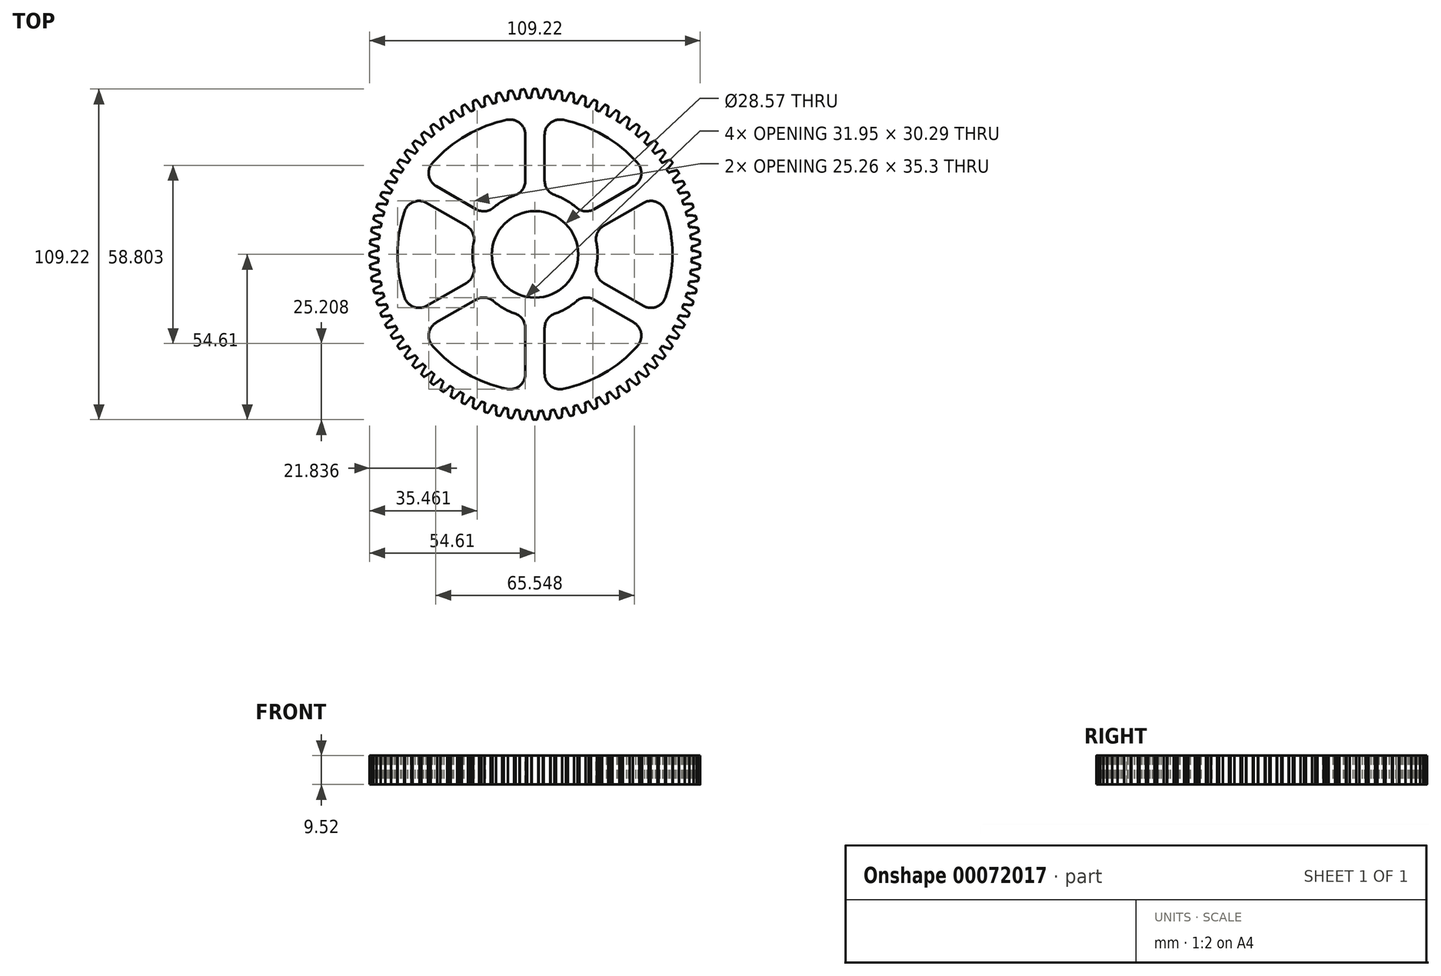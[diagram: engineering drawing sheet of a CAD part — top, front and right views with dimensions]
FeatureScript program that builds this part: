
annotation { "Feature Type Name" : "Feature", "Feature Type Description" : "" }
export const myFeature = defineFeature(function(context is Context, id is Id, definition is map)
    precondition{}
    {
        {
            var Q0;
            Q0=qCreatedBy(makeId("Top.planeOp"),FACE);
            var sketch = newSketch(context, id + "F0", { "sketchPlane" : qUnion([Q0])});
            skArc(sketch, "E0", {"start": v(1.25, 51.74) * mm, "mid": v(0, 51.75) * mm, "end": v(-1.25, 51.74) * mm});
            skArc(sketch, "E1", {"start": v(-1.25, -51.74) * mm, "mid": v(51.74, -1.25) * mm, "end": v(1.25, 51.74) * mm});
            skArc(sketch, "E2", {"start": v(-1.05, 53.12) * mm, "mid": v(-1.2, 52.43) * mm, "end": v(-1.25, 51.74) * mm});
            skArc(sketch, "E3", {"start": v(-0.67, 54.46) * mm, "mid": v(-0.86, 53.79) * mm, "end": v(-1.05, 53.12) * mm});
            skArc(sketch, "E4", {"start": v(-0.48, 54.6) * mm, "mid": v(-0.6, 54.57) * mm, "end": v(-0.67, 54.46) * mm});
            skArc(sketch, "E5", {"start": v(1.25, 51.74) * mm, "mid": v(1.2, 52.43) * mm, "end": v(1.05, 53.12) * mm});
            skArc(sketch, "E6", {"start": v(1.05, 53.12) * mm, "mid": v(0.86, 53.79) * mm, "end": v(0.67, 54.46) * mm});
            skArc(sketch, "E7", {"start": v(0.48, 54.6) * mm, "mid": v(0, 54.61) * mm, "end": v(-0.48, 54.6) * mm});
            skArc(sketch, "E8", {"start": v(0.67, 54.46) * mm, "mid": v(0.6, 54.57) * mm, "end": v(0.48, 54.6) * mm});
            skArc(sketch, "E9", {"start": v(-1.25, 51.74) * mm, "mid": v(-51.75, 0) * mm, "end": v(-1.25, -51.74) * mm});
            skSolve(sketch);
        }
        {
            var Q0;
            Q0=makeQuery(id+"F0.imprint","IMPRINT",FACE,{"disambiguationData":[TD([[makeQuery(id+"F0.imprint","IMPRINT",EDGE,{"derivedFrom":sQuery(id+"F0.wireOp",EDGE,"E0")}),1.0]])]});
            extrude(context, id + "F1", {"entities" : qUnion([Q0]), "endBound" : BoundingType.SYMMETRIC, "depth" : 9.52 * mm});
        }
        {
            var Q0;
            {var subQ0=sQuery(id+"F0.wireOp",EDGE,"E0");Q0=makeQuery(id+"F0.imprint","IMPRINT",FACE,{"disambiguationData":[TD([[makeQuery(id+"F0.imprint","IMPRINT",EDGE,{"derivedFrom":subQ0}),-1.0]])]});}
            var Q1;
            Q1=makeQuery(id+"F1.opExtrude","CAP_FACE",FACE,{"disambiguationData":[OSD([sQuery(id+"F0.wireOp",EDGE,"E0"),sQuery(id+"F0.wireOp",EDGE,"E1"),sQuery(id+"F0.wireOp",EDGE,"E9")])],"isStart":false});
            var Q2;
            Q2=makeQuery(id+"F1.opExtrude","CAP_FACE",FACE,{"disambiguationData":[OSD([sQuery(id+"F0.wireOp",EDGE,"E0"),sQuery(id+"F0.wireOp",EDGE,"E1"),sQuery(id+"F0.wireOp",EDGE,"E9")])],"isStart":true});
            extrude(context, id + "F2", {"entities" : qUnion([Q0]), "endBound" : BoundingType.UP_TO_SURFACE, "endBoundEntityFace" : qUnion([Q1]), "depth" : 25.4 * mm, "hasSecondDirection" : true, "secondDirectionBound" : SecondDirectionBoundingType.UP_TO_SURFACE, "secondDirectionOppositeDirection" : true, "secondDirectionBoundEntityFace" : qUnion([Q2]), "secondDirectionDepth" : 25.4 * mm});
        }
        {
            var Q0;
            Q0=makeQuery(id+"F2.opExtrude","SWEPT_BODY",BODY,{"disambiguationData":[OSD([sQuery(id+"F0.wireOp",EDGE,"E0"),sQuery(id+"F0.wireOp",EDGE,"E2"),sQuery(id+"F0.wireOp",EDGE,"E3"),sQuery(id+"F0.wireOp",EDGE,"E4"),sQuery(id+"F0.wireOp",EDGE,"E5"),sQuery(id+"F0.wireOp",EDGE,"E6"),sQuery(id+"F0.wireOp",EDGE,"E7"),sQuery(id+"F0.wireOp",EDGE,"E8")])]});
            var Q1;
            Q1=makeQuery(id+"F1.opExtrude","SWEPT_FACE",FACE,{"disambiguationData":[OSD([sQuery(id+"F0.wireOp",EDGE,"E0"),sQuery(id+"F0.wireOp",EDGE,"E1"),sQuery(id+"F0.wireOp",EDGE,"E9")])]});
            circularPattern(context, id + "F3", {"operationType" : NewBodyOperationType.ADD, "entities" : qUnion([Q0]), "axis" : qUnion([Q1]), "angle" : 360 * degree, "instanceCount" : round(84), "equalSpace" : true});
        }
        {
            var Q0;
            {var subQ0=sQuery(id+"F0.wireOp",EDGE,"E0");var subQ1=makeQuery(id+"F2.opExtrude","CAP_FACE",FACE,{"disambiguationData":[OSD([subQ0,sQuery(id+"F0.wireOp",EDGE,"E2"),sQuery(id+"F0.wireOp",EDGE,"E3"),sQuery(id+"F0.wireOp",EDGE,"E4"),sQuery(id+"F0.wireOp",EDGE,"E5"),sQuery(id+"F0.wireOp",EDGE,"E6"),sQuery(id+"F0.wireOp",EDGE,"E7"),sQuery(id+"F0.wireOp",EDGE,"E8")])],"isStart":false});Q0=makeQuery(id+"F3.boolean.opBoolean","MERGE",FACE,{"derivedFrom":[makeQuery(id+"F1.opExtrude","CAP_FACE",FACE,{"disambiguationData":[OSD([subQ0,sQuery(id+"F0.wireOp",EDGE,"E1"),sQuery(id+"F0.wireOp",EDGE,"E9")])],"isStart":false}),subQ1,makeQuery(id+"F3.opPattern","COPY",FACE,{"derivedFrom":subQ1,"instanceName":"1"}),makeQuery(id+"F3.opPattern","COPY",FACE,{"derivedFrom":subQ1,"instanceName":"2"}),makeQuery(id+"F3.opPattern","COPY",FACE,{"derivedFrom":subQ1,"instanceName":"3"}),makeQuery(id+"F3.opPattern","COPY",FACE,{"derivedFrom":subQ1,"instanceName":"4"}),makeQuery(id+"F3.opPattern","COPY",FACE,{"derivedFrom":subQ1,"instanceName":"5"}),makeQuery(id+"F3.opPattern","COPY",FACE,{"derivedFrom":subQ1,"instanceName":"6"}),makeQuery(id+"F3.opPattern","COPY",FACE,{"derivedFrom":subQ1,"instanceName":"7"}),makeQuery(id+"F3.opPattern","COPY",FACE,{"derivedFrom":subQ1,"instanceName":"8"}),makeQuery(id+"F3.opPattern","COPY",FACE,{"derivedFrom":subQ1,"instanceName":"9"}),makeQuery(id+"F3.opPattern","COPY",FACE,{"derivedFrom":subQ1,"instanceName":"10"}),makeQuery(id+"F3.opPattern","COPY",FACE,{"derivedFrom":subQ1,"instanceName":"11"}),makeQuery(id+"F3.opPattern","COPY",FACE,{"derivedFrom":subQ1,"instanceName":"12"}),makeQuery(id+"F3.opPattern","COPY",FACE,{"derivedFrom":subQ1,"instanceName":"13"}),makeQuery(id+"F3.opPattern","COPY",FACE,{"derivedFrom":subQ1,"instanceName":"14"}),makeQuery(id+"F3.opPattern","COPY",FACE,{"derivedFrom":subQ1,"instanceName":"15"}),makeQuery(id+"F3.opPattern","COPY",FACE,{"derivedFrom":subQ1,"instanceName":"16"}),makeQuery(id+"F3.opPattern","COPY",FACE,{"derivedFrom":subQ1,"instanceName":"17"}),makeQuery(id+"F3.opPattern","COPY",FACE,{"derivedFrom":subQ1,"instanceName":"18"}),makeQuery(id+"F3.opPattern","COPY",FACE,{"derivedFrom":subQ1,"instanceName":"19"}),makeQuery(id+"F3.opPattern","COPY",FACE,{"derivedFrom":subQ1,"instanceName":"20"}),makeQuery(id+"F3.opPattern","COPY",FACE,{"derivedFrom":subQ1,"instanceName":"21"}),makeQuery(id+"F3.opPattern","COPY",FACE,{"derivedFrom":subQ1,"instanceName":"22"}),makeQuery(id+"F3.opPattern","COPY",FACE,{"derivedFrom":subQ1,"instanceName":"23"}),makeQuery(id+"F3.opPattern","COPY",FACE,{"derivedFrom":subQ1,"instanceName":"24"}),makeQuery(id+"F3.opPattern","COPY",FACE,{"derivedFrom":subQ1,"instanceName":"25"}),makeQuery(id+"F3.opPattern","COPY",FACE,{"derivedFrom":subQ1,"instanceName":"26"}),makeQuery(id+"F3.opPattern","COPY",FACE,{"derivedFrom":subQ1,"instanceName":"27"}),makeQuery(id+"F3.opPattern","COPY",FACE,{"derivedFrom":subQ1,"instanceName":"28"}),makeQuery(id+"F3.opPattern","COPY",FACE,{"derivedFrom":subQ1,"instanceName":"29"}),makeQuery(id+"F3.opPattern","COPY",FACE,{"derivedFrom":subQ1,"instanceName":"30"}),makeQuery(id+"F3.opPattern","COPY",FACE,{"derivedFrom":subQ1,"instanceName":"31"}),makeQuery(id+"F3.opPattern","COPY",FACE,{"derivedFrom":subQ1,"instanceName":"32"}),makeQuery(id+"F3.opPattern","COPY",FACE,{"derivedFrom":subQ1,"instanceName":"33"}),makeQuery(id+"F3.opPattern","COPY",FACE,{"derivedFrom":subQ1,"instanceName":"34"}),makeQuery(id+"F3.opPattern","COPY",FACE,{"derivedFrom":subQ1,"instanceName":"35"}),makeQuery(id+"F3.opPattern","COPY",FACE,{"derivedFrom":subQ1,"instanceName":"36"}),makeQuery(id+"F3.opPattern","COPY",FACE,{"derivedFrom":subQ1,"instanceName":"37"}),makeQuery(id+"F3.opPattern","COPY",FACE,{"derivedFrom":subQ1,"instanceName":"38"}),makeQuery(id+"F3.opPattern","COPY",FACE,{"derivedFrom":subQ1,"instanceName":"39"}),makeQuery(id+"F3.opPattern","COPY",FACE,{"derivedFrom":subQ1,"instanceName":"40"}),makeQuery(id+"F3.opPattern","COPY",FACE,{"derivedFrom":subQ1,"instanceName":"41"}),makeQuery(id+"F3.opPattern","COPY",FACE,{"derivedFrom":subQ1,"instanceName":"42"}),makeQuery(id+"F3.opPattern","COPY",FACE,{"derivedFrom":subQ1,"instanceName":"43"}),makeQuery(id+"F3.opPattern","COPY",FACE,{"derivedFrom":subQ1,"instanceName":"44"}),makeQuery(id+"F3.opPattern","COPY",FACE,{"derivedFrom":subQ1,"instanceName":"45"}),makeQuery(id+"F3.opPattern","COPY",FACE,{"derivedFrom":subQ1,"instanceName":"46"}),makeQuery(id+"F3.opPattern","COPY",FACE,{"derivedFrom":subQ1,"instanceName":"47"}),makeQuery(id+"F3.opPattern","COPY",FACE,{"derivedFrom":subQ1,"instanceName":"48"}),makeQuery(id+"F3.opPattern","COPY",FACE,{"derivedFrom":subQ1,"instanceName":"49"}),makeQuery(id+"F3.opPattern","COPY",FACE,{"derivedFrom":subQ1,"instanceName":"50"}),makeQuery(id+"F3.opPattern","COPY",FACE,{"derivedFrom":subQ1,"instanceName":"51"}),makeQuery(id+"F3.opPattern","COPY",FACE,{"derivedFrom":subQ1,"instanceName":"52"}),makeQuery(id+"F3.opPattern","COPY",FACE,{"derivedFrom":subQ1,"instanceName":"53"}),makeQuery(id+"F3.opPattern","COPY",FACE,{"derivedFrom":subQ1,"instanceName":"54"}),makeQuery(id+"F3.opPattern","COPY",FACE,{"derivedFrom":subQ1,"instanceName":"55"}),makeQuery(id+"F3.opPattern","COPY",FACE,{"derivedFrom":subQ1,"instanceName":"56"}),makeQuery(id+"F3.opPattern","COPY",FACE,{"derivedFrom":subQ1,"instanceName":"57"}),makeQuery(id+"F3.opPattern","COPY",FACE,{"derivedFrom":subQ1,"instanceName":"58"}),makeQuery(id+"F3.opPattern","COPY",FACE,{"derivedFrom":subQ1,"instanceName":"59"}),makeQuery(id+"F3.opPattern","COPY",FACE,{"derivedFrom":subQ1,"instanceName":"60"}),makeQuery(id+"F3.opPattern","COPY",FACE,{"derivedFrom":subQ1,"instanceName":"61"}),makeQuery(id+"F3.opPattern","COPY",FACE,{"derivedFrom":subQ1,"instanceName":"62"}),makeQuery(id+"F3.opPattern","COPY",FACE,{"derivedFrom":subQ1,"instanceName":"63"}),makeQuery(id+"F3.opPattern","COPY",FACE,{"derivedFrom":subQ1,"instanceName":"64"}),makeQuery(id+"F3.opPattern","COPY",FACE,{"derivedFrom":subQ1,"instanceName":"65"}),makeQuery(id+"F3.opPattern","COPY",FACE,{"derivedFrom":subQ1,"instanceName":"66"}),makeQuery(id+"F3.opPattern","COPY",FACE,{"derivedFrom":subQ1,"instanceName":"67"}),makeQuery(id+"F3.opPattern","COPY",FACE,{"derivedFrom":subQ1,"instanceName":"68"}),makeQuery(id+"F3.opPattern","COPY",FACE,{"derivedFrom":subQ1,"instanceName":"69"}),makeQuery(id+"F3.opPattern","COPY",FACE,{"derivedFrom":subQ1,"instanceName":"70"}),makeQuery(id+"F3.opPattern","COPY",FACE,{"derivedFrom":subQ1,"instanceName":"71"}),makeQuery(id+"F3.opPattern","COPY",FACE,{"derivedFrom":subQ1,"instanceName":"72"}),makeQuery(id+"F3.opPattern","COPY",FACE,{"derivedFrom":subQ1,"instanceName":"73"}),makeQuery(id+"F3.opPattern","COPY",FACE,{"derivedFrom":subQ1,"instanceName":"74"}),makeQuery(id+"F3.opPattern","COPY",FACE,{"derivedFrom":subQ1,"instanceName":"75"}),makeQuery(id+"F3.opPattern","COPY",FACE,{"derivedFrom":subQ1,"instanceName":"76"}),makeQuery(id+"F3.opPattern","COPY",FACE,{"derivedFrom":subQ1,"instanceName":"77"}),makeQuery(id+"F3.opPattern","COPY",FACE,{"derivedFrom":subQ1,"instanceName":"78"}),makeQuery(id+"F3.opPattern","COPY",FACE,{"derivedFrom":subQ1,"instanceName":"79"}),makeQuery(id+"F3.opPattern","COPY",FACE,{"derivedFrom":subQ1,"instanceName":"80"}),makeQuery(id+"F3.opPattern","COPY",FACE,{"derivedFrom":subQ1,"instanceName":"81"}),makeQuery(id+"F3.opPattern","COPY",FACE,{"derivedFrom":subQ1,"instanceName":"82"}),makeQuery(id+"F3.opPattern","COPY",FACE,{"derivedFrom":subQ1,"instanceName":"83"})]});}
            var sketch = newSketch(context, id + "F4", { "sketchPlane" : qUnion([Q0])});
            skCircle(sketch, "E10", {"center": v(0, 0) * mm, "radius": 14.29 * mm});
            skSolve(sketch);
        }
        {
            var Q0;
            Q0=makeQuery(id+"F4.imprint","IMPRINT",FACE,{"disambiguationData":[TD([[makeQuery(id+"F4.imprint","IMPRINT",EDGE,{"derivedFrom":sQuery(id+"F4.wireOp",EDGE,"E10")}),1.0]])]});
            extrude(context, id + "F5", {"entities" : qUnion([Q0]), "operationType" : NewBodyOperationType.REMOVE, "endBound" : BoundingType.UP_TO_NEXT, "oppositeDirection" : true, "depth" : 25.4 * mm});
        }
        {
            var Q0;
            {var subQ0=sQuery(id+"F0.wireOp",EDGE,"E0");var subQ1=makeQuery(id+"F2.opExtrude","CAP_FACE",FACE,{"disambiguationData":[OSD([subQ0,sQuery(id+"F0.wireOp",EDGE,"E2"),sQuery(id+"F0.wireOp",EDGE,"E3"),sQuery(id+"F0.wireOp",EDGE,"E4"),sQuery(id+"F0.wireOp",EDGE,"E5"),sQuery(id+"F0.wireOp",EDGE,"E6"),sQuery(id+"F0.wireOp",EDGE,"E7"),sQuery(id+"F0.wireOp",EDGE,"E8")])],"isStart":false});Q0=makeQuery(id+"F3.boolean.opBoolean","MERGE",FACE,{"derivedFrom":[makeQuery(id+"F1.opExtrude","CAP_FACE",FACE,{"disambiguationData":[OSD([subQ0,sQuery(id+"F0.wireOp",EDGE,"E1"),sQuery(id+"F0.wireOp",EDGE,"E9")])],"isStart":false}),subQ1,makeQuery(id+"F3.opPattern","COPY",FACE,{"derivedFrom":subQ1,"instanceName":"1"}),makeQuery(id+"F3.opPattern","COPY",FACE,{"derivedFrom":subQ1,"instanceName":"2"}),makeQuery(id+"F3.opPattern","COPY",FACE,{"derivedFrom":subQ1,"instanceName":"3"}),makeQuery(id+"F3.opPattern","COPY",FACE,{"derivedFrom":subQ1,"instanceName":"4"}),makeQuery(id+"F3.opPattern","COPY",FACE,{"derivedFrom":subQ1,"instanceName":"5"}),makeQuery(id+"F3.opPattern","COPY",FACE,{"derivedFrom":subQ1,"instanceName":"6"}),makeQuery(id+"F3.opPattern","COPY",FACE,{"derivedFrom":subQ1,"instanceName":"7"}),makeQuery(id+"F3.opPattern","COPY",FACE,{"derivedFrom":subQ1,"instanceName":"8"}),makeQuery(id+"F3.opPattern","COPY",FACE,{"derivedFrom":subQ1,"instanceName":"9"}),makeQuery(id+"F3.opPattern","COPY",FACE,{"derivedFrom":subQ1,"instanceName":"10"}),makeQuery(id+"F3.opPattern","COPY",FACE,{"derivedFrom":subQ1,"instanceName":"11"}),makeQuery(id+"F3.opPattern","COPY",FACE,{"derivedFrom":subQ1,"instanceName":"12"}),makeQuery(id+"F3.opPattern","COPY",FACE,{"derivedFrom":subQ1,"instanceName":"13"}),makeQuery(id+"F3.opPattern","COPY",FACE,{"derivedFrom":subQ1,"instanceName":"14"}),makeQuery(id+"F3.opPattern","COPY",FACE,{"derivedFrom":subQ1,"instanceName":"15"}),makeQuery(id+"F3.opPattern","COPY",FACE,{"derivedFrom":subQ1,"instanceName":"16"}),makeQuery(id+"F3.opPattern","COPY",FACE,{"derivedFrom":subQ1,"instanceName":"17"}),makeQuery(id+"F3.opPattern","COPY",FACE,{"derivedFrom":subQ1,"instanceName":"18"}),makeQuery(id+"F3.opPattern","COPY",FACE,{"derivedFrom":subQ1,"instanceName":"19"}),makeQuery(id+"F3.opPattern","COPY",FACE,{"derivedFrom":subQ1,"instanceName":"20"}),makeQuery(id+"F3.opPattern","COPY",FACE,{"derivedFrom":subQ1,"instanceName":"21"}),makeQuery(id+"F3.opPattern","COPY",FACE,{"derivedFrom":subQ1,"instanceName":"22"}),makeQuery(id+"F3.opPattern","COPY",FACE,{"derivedFrom":subQ1,"instanceName":"23"}),makeQuery(id+"F3.opPattern","COPY",FACE,{"derivedFrom":subQ1,"instanceName":"24"}),makeQuery(id+"F3.opPattern","COPY",FACE,{"derivedFrom":subQ1,"instanceName":"25"}),makeQuery(id+"F3.opPattern","COPY",FACE,{"derivedFrom":subQ1,"instanceName":"26"}),makeQuery(id+"F3.opPattern","COPY",FACE,{"derivedFrom":subQ1,"instanceName":"27"}),makeQuery(id+"F3.opPattern","COPY",FACE,{"derivedFrom":subQ1,"instanceName":"28"}),makeQuery(id+"F3.opPattern","COPY",FACE,{"derivedFrom":subQ1,"instanceName":"29"}),makeQuery(id+"F3.opPattern","COPY",FACE,{"derivedFrom":subQ1,"instanceName":"30"}),makeQuery(id+"F3.opPattern","COPY",FACE,{"derivedFrom":subQ1,"instanceName":"31"}),makeQuery(id+"F3.opPattern","COPY",FACE,{"derivedFrom":subQ1,"instanceName":"32"}),makeQuery(id+"F3.opPattern","COPY",FACE,{"derivedFrom":subQ1,"instanceName":"33"}),makeQuery(id+"F3.opPattern","COPY",FACE,{"derivedFrom":subQ1,"instanceName":"34"}),makeQuery(id+"F3.opPattern","COPY",FACE,{"derivedFrom":subQ1,"instanceName":"35"}),makeQuery(id+"F3.opPattern","COPY",FACE,{"derivedFrom":subQ1,"instanceName":"36"}),makeQuery(id+"F3.opPattern","COPY",FACE,{"derivedFrom":subQ1,"instanceName":"37"}),makeQuery(id+"F3.opPattern","COPY",FACE,{"derivedFrom":subQ1,"instanceName":"38"}),makeQuery(id+"F3.opPattern","COPY",FACE,{"derivedFrom":subQ1,"instanceName":"39"}),makeQuery(id+"F3.opPattern","COPY",FACE,{"derivedFrom":subQ1,"instanceName":"40"}),makeQuery(id+"F3.opPattern","COPY",FACE,{"derivedFrom":subQ1,"instanceName":"41"}),makeQuery(id+"F3.opPattern","COPY",FACE,{"derivedFrom":subQ1,"instanceName":"42"}),makeQuery(id+"F3.opPattern","COPY",FACE,{"derivedFrom":subQ1,"instanceName":"43"}),makeQuery(id+"F3.opPattern","COPY",FACE,{"derivedFrom":subQ1,"instanceName":"44"}),makeQuery(id+"F3.opPattern","COPY",FACE,{"derivedFrom":subQ1,"instanceName":"45"}),makeQuery(id+"F3.opPattern","COPY",FACE,{"derivedFrom":subQ1,"instanceName":"46"}),makeQuery(id+"F3.opPattern","COPY",FACE,{"derivedFrom":subQ1,"instanceName":"47"}),makeQuery(id+"F3.opPattern","COPY",FACE,{"derivedFrom":subQ1,"instanceName":"48"}),makeQuery(id+"F3.opPattern","COPY",FACE,{"derivedFrom":subQ1,"instanceName":"49"}),makeQuery(id+"F3.opPattern","COPY",FACE,{"derivedFrom":subQ1,"instanceName":"50"}),makeQuery(id+"F3.opPattern","COPY",FACE,{"derivedFrom":subQ1,"instanceName":"51"}),makeQuery(id+"F3.opPattern","COPY",FACE,{"derivedFrom":subQ1,"instanceName":"52"}),makeQuery(id+"F3.opPattern","COPY",FACE,{"derivedFrom":subQ1,"instanceName":"53"}),makeQuery(id+"F3.opPattern","COPY",FACE,{"derivedFrom":subQ1,"instanceName":"54"}),makeQuery(id+"F3.opPattern","COPY",FACE,{"derivedFrom":subQ1,"instanceName":"55"}),makeQuery(id+"F3.opPattern","COPY",FACE,{"derivedFrom":subQ1,"instanceName":"56"}),makeQuery(id+"F3.opPattern","COPY",FACE,{"derivedFrom":subQ1,"instanceName":"57"}),makeQuery(id+"F3.opPattern","COPY",FACE,{"derivedFrom":subQ1,"instanceName":"58"}),makeQuery(id+"F3.opPattern","COPY",FACE,{"derivedFrom":subQ1,"instanceName":"59"}),makeQuery(id+"F3.opPattern","COPY",FACE,{"derivedFrom":subQ1,"instanceName":"60"}),makeQuery(id+"F3.opPattern","COPY",FACE,{"derivedFrom":subQ1,"instanceName":"61"}),makeQuery(id+"F3.opPattern","COPY",FACE,{"derivedFrom":subQ1,"instanceName":"62"}),makeQuery(id+"F3.opPattern","COPY",FACE,{"derivedFrom":subQ1,"instanceName":"63"}),makeQuery(id+"F3.opPattern","COPY",FACE,{"derivedFrom":subQ1,"instanceName":"64"}),makeQuery(id+"F3.opPattern","COPY",FACE,{"derivedFrom":subQ1,"instanceName":"65"}),makeQuery(id+"F3.opPattern","COPY",FACE,{"derivedFrom":subQ1,"instanceName":"66"}),makeQuery(id+"F3.opPattern","COPY",FACE,{"derivedFrom":subQ1,"instanceName":"67"}),makeQuery(id+"F3.opPattern","COPY",FACE,{"derivedFrom":subQ1,"instanceName":"68"}),makeQuery(id+"F3.opPattern","COPY",FACE,{"derivedFrom":subQ1,"instanceName":"69"}),makeQuery(id+"F3.opPattern","COPY",FACE,{"derivedFrom":subQ1,"instanceName":"70"}),makeQuery(id+"F3.opPattern","COPY",FACE,{"derivedFrom":subQ1,"instanceName":"71"}),makeQuery(id+"F3.opPattern","COPY",FACE,{"derivedFrom":subQ1,"instanceName":"72"}),makeQuery(id+"F3.opPattern","COPY",FACE,{"derivedFrom":subQ1,"instanceName":"73"}),makeQuery(id+"F3.opPattern","COPY",FACE,{"derivedFrom":subQ1,"instanceName":"74"}),makeQuery(id+"F3.opPattern","COPY",FACE,{"derivedFrom":subQ1,"instanceName":"75"}),makeQuery(id+"F3.opPattern","COPY",FACE,{"derivedFrom":subQ1,"instanceName":"76"}),makeQuery(id+"F3.opPattern","COPY",FACE,{"derivedFrom":subQ1,"instanceName":"77"}),makeQuery(id+"F3.opPattern","COPY",FACE,{"derivedFrom":subQ1,"instanceName":"78"}),makeQuery(id+"F3.opPattern","COPY",FACE,{"derivedFrom":subQ1,"instanceName":"79"}),makeQuery(id+"F3.opPattern","COPY",FACE,{"derivedFrom":subQ1,"instanceName":"80"}),makeQuery(id+"F3.opPattern","COPY",FACE,{"derivedFrom":subQ1,"instanceName":"81"}),makeQuery(id+"F3.opPattern","COPY",FACE,{"derivedFrom":subQ1,"instanceName":"82"}),makeQuery(id+"F3.opPattern","COPY",FACE,{"derivedFrom":subQ1,"instanceName":"83"})]});}
            var sketch = newSketch(context, id + "F6", { "sketchPlane" : qUnion([Q0])});
            skArc(sketch, "E11", {"start": v(0, 20.64) * mm, "mid": v(-10.32, 17.87) * mm, "end": v(-17.87, 10.32) * mm});
            skArc(sketch, "E12", {"start": v(0, 45.4) * mm, "mid": v(-22.7, 39.32) * mm, "end": v(-39.32, 22.7) * mm});
            skLineSegment(sketch, "E13", {"start": v(0, 20.64) * mm, "end": v(0, 45.4) * mm, "construction": true});
            skLineSegment(sketch, "E14", {"start": v(-17.87, 10.32) * mm, "end": v(-39.32, 22.7) * mm, "construction": true});
            skLineSegment(sketch, "E15.0", {"start": v(-16.07, 12.95) * mm, "end": v(-37.64, 25.4) * mm});
            skLineSegment(sketch, "E16.0", {"start": v(-3.18, 20.4) * mm, "end": v(-3.18, 45.3) * mm});
            skSolve(sketch);
        }
        {
            var Q0;
            {var subQ0=sQuery(id+"F6.wireOp",EDGE,"E15.0");Q0=makeQuery(id+"F6.imprint","IMPRINT",FACE,{"disambiguationData":[TD([[makeQuery(id+"F6.imprint","IMPRINT",EDGE,{"derivedFrom":subQ0}),-1.0]])]});}
            var Q1;
            {var subQ0=sQuery(id+"F0.wireOp",EDGE,"E0");var subQ1=makeQuery(id+"F2.opExtrude","CAP_FACE",FACE,{"disambiguationData":[OSD([subQ0,sQuery(id+"F0.wireOp",EDGE,"E2"),sQuery(id+"F0.wireOp",EDGE,"E3"),sQuery(id+"F0.wireOp",EDGE,"E4"),sQuery(id+"F0.wireOp",EDGE,"E5"),sQuery(id+"F0.wireOp",EDGE,"E6"),sQuery(id+"F0.wireOp",EDGE,"E7"),sQuery(id+"F0.wireOp",EDGE,"E8")])],"isStart":true});Q1=makeQuery(id+"F3.boolean.opBoolean","MERGE",FACE,{"derivedFrom":[makeQuery(id+"F1.opExtrude","CAP_FACE",FACE,{"disambiguationData":[OSD([subQ0,sQuery(id+"F0.wireOp",EDGE,"E1"),sQuery(id+"F0.wireOp",EDGE,"E9")])],"isStart":true}),subQ1,makeQuery(id+"F3.opPattern","COPY",FACE,{"derivedFrom":subQ1,"instanceName":"1"}),makeQuery(id+"F3.opPattern","COPY",FACE,{"derivedFrom":subQ1,"instanceName":"2"}),makeQuery(id+"F3.opPattern","COPY",FACE,{"derivedFrom":subQ1,"instanceName":"3"}),makeQuery(id+"F3.opPattern","COPY",FACE,{"derivedFrom":subQ1,"instanceName":"4"}),makeQuery(id+"F3.opPattern","COPY",FACE,{"derivedFrom":subQ1,"instanceName":"5"}),makeQuery(id+"F3.opPattern","COPY",FACE,{"derivedFrom":subQ1,"instanceName":"6"}),makeQuery(id+"F3.opPattern","COPY",FACE,{"derivedFrom":subQ1,"instanceName":"7"}),makeQuery(id+"F3.opPattern","COPY",FACE,{"derivedFrom":subQ1,"instanceName":"8"}),makeQuery(id+"F3.opPattern","COPY",FACE,{"derivedFrom":subQ1,"instanceName":"9"}),makeQuery(id+"F3.opPattern","COPY",FACE,{"derivedFrom":subQ1,"instanceName":"10"}),makeQuery(id+"F3.opPattern","COPY",FACE,{"derivedFrom":subQ1,"instanceName":"11"}),makeQuery(id+"F3.opPattern","COPY",FACE,{"derivedFrom":subQ1,"instanceName":"12"}),makeQuery(id+"F3.opPattern","COPY",FACE,{"derivedFrom":subQ1,"instanceName":"13"}),makeQuery(id+"F3.opPattern","COPY",FACE,{"derivedFrom":subQ1,"instanceName":"14"}),makeQuery(id+"F3.opPattern","COPY",FACE,{"derivedFrom":subQ1,"instanceName":"15"}),makeQuery(id+"F3.opPattern","COPY",FACE,{"derivedFrom":subQ1,"instanceName":"16"}),makeQuery(id+"F3.opPattern","COPY",FACE,{"derivedFrom":subQ1,"instanceName":"17"}),makeQuery(id+"F3.opPattern","COPY",FACE,{"derivedFrom":subQ1,"instanceName":"18"}),makeQuery(id+"F3.opPattern","COPY",FACE,{"derivedFrom":subQ1,"instanceName":"19"}),makeQuery(id+"F3.opPattern","COPY",FACE,{"derivedFrom":subQ1,"instanceName":"20"}),makeQuery(id+"F3.opPattern","COPY",FACE,{"derivedFrom":subQ1,"instanceName":"21"}),makeQuery(id+"F3.opPattern","COPY",FACE,{"derivedFrom":subQ1,"instanceName":"22"}),makeQuery(id+"F3.opPattern","COPY",FACE,{"derivedFrom":subQ1,"instanceName":"23"}),makeQuery(id+"F3.opPattern","COPY",FACE,{"derivedFrom":subQ1,"instanceName":"24"}),makeQuery(id+"F3.opPattern","COPY",FACE,{"derivedFrom":subQ1,"instanceName":"25"}),makeQuery(id+"F3.opPattern","COPY",FACE,{"derivedFrom":subQ1,"instanceName":"26"}),makeQuery(id+"F3.opPattern","COPY",FACE,{"derivedFrom":subQ1,"instanceName":"27"}),makeQuery(id+"F3.opPattern","COPY",FACE,{"derivedFrom":subQ1,"instanceName":"28"}),makeQuery(id+"F3.opPattern","COPY",FACE,{"derivedFrom":subQ1,"instanceName":"29"}),makeQuery(id+"F3.opPattern","COPY",FACE,{"derivedFrom":subQ1,"instanceName":"30"}),makeQuery(id+"F3.opPattern","COPY",FACE,{"derivedFrom":subQ1,"instanceName":"31"}),makeQuery(id+"F3.opPattern","COPY",FACE,{"derivedFrom":subQ1,"instanceName":"32"}),makeQuery(id+"F3.opPattern","COPY",FACE,{"derivedFrom":subQ1,"instanceName":"33"}),makeQuery(id+"F3.opPattern","COPY",FACE,{"derivedFrom":subQ1,"instanceName":"34"}),makeQuery(id+"F3.opPattern","COPY",FACE,{"derivedFrom":subQ1,"instanceName":"35"}),makeQuery(id+"F3.opPattern","COPY",FACE,{"derivedFrom":subQ1,"instanceName":"36"}),makeQuery(id+"F3.opPattern","COPY",FACE,{"derivedFrom":subQ1,"instanceName":"37"}),makeQuery(id+"F3.opPattern","COPY",FACE,{"derivedFrom":subQ1,"instanceName":"38"}),makeQuery(id+"F3.opPattern","COPY",FACE,{"derivedFrom":subQ1,"instanceName":"39"}),makeQuery(id+"F3.opPattern","COPY",FACE,{"derivedFrom":subQ1,"instanceName":"40"}),makeQuery(id+"F3.opPattern","COPY",FACE,{"derivedFrom":subQ1,"instanceName":"41"}),makeQuery(id+"F3.opPattern","COPY",FACE,{"derivedFrom":subQ1,"instanceName":"42"}),makeQuery(id+"F3.opPattern","COPY",FACE,{"derivedFrom":subQ1,"instanceName":"43"}),makeQuery(id+"F3.opPattern","COPY",FACE,{"derivedFrom":subQ1,"instanceName":"44"}),makeQuery(id+"F3.opPattern","COPY",FACE,{"derivedFrom":subQ1,"instanceName":"45"}),makeQuery(id+"F3.opPattern","COPY",FACE,{"derivedFrom":subQ1,"instanceName":"46"}),makeQuery(id+"F3.opPattern","COPY",FACE,{"derivedFrom":subQ1,"instanceName":"47"}),makeQuery(id+"F3.opPattern","COPY",FACE,{"derivedFrom":subQ1,"instanceName":"48"}),makeQuery(id+"F3.opPattern","COPY",FACE,{"derivedFrom":subQ1,"instanceName":"49"}),makeQuery(id+"F3.opPattern","COPY",FACE,{"derivedFrom":subQ1,"instanceName":"50"}),makeQuery(id+"F3.opPattern","COPY",FACE,{"derivedFrom":subQ1,"instanceName":"51"}),makeQuery(id+"F3.opPattern","COPY",FACE,{"derivedFrom":subQ1,"instanceName":"52"}),makeQuery(id+"F3.opPattern","COPY",FACE,{"derivedFrom":subQ1,"instanceName":"53"}),makeQuery(id+"F3.opPattern","COPY",FACE,{"derivedFrom":subQ1,"instanceName":"54"}),makeQuery(id+"F3.opPattern","COPY",FACE,{"derivedFrom":subQ1,"instanceName":"55"}),makeQuery(id+"F3.opPattern","COPY",FACE,{"derivedFrom":subQ1,"instanceName":"56"}),makeQuery(id+"F3.opPattern","COPY",FACE,{"derivedFrom":subQ1,"instanceName":"57"}),makeQuery(id+"F3.opPattern","COPY",FACE,{"derivedFrom":subQ1,"instanceName":"58"}),makeQuery(id+"F3.opPattern","COPY",FACE,{"derivedFrom":subQ1,"instanceName":"59"}),makeQuery(id+"F3.opPattern","COPY",FACE,{"derivedFrom":subQ1,"instanceName":"60"}),makeQuery(id+"F3.opPattern","COPY",FACE,{"derivedFrom":subQ1,"instanceName":"61"}),makeQuery(id+"F3.opPattern","COPY",FACE,{"derivedFrom":subQ1,"instanceName":"62"}),makeQuery(id+"F3.opPattern","COPY",FACE,{"derivedFrom":subQ1,"instanceName":"63"}),makeQuery(id+"F3.opPattern","COPY",FACE,{"derivedFrom":subQ1,"instanceName":"64"}),makeQuery(id+"F3.opPattern","COPY",FACE,{"derivedFrom":subQ1,"instanceName":"65"}),makeQuery(id+"F3.opPattern","COPY",FACE,{"derivedFrom":subQ1,"instanceName":"66"}),makeQuery(id+"F3.opPattern","COPY",FACE,{"derivedFrom":subQ1,"instanceName":"67"}),makeQuery(id+"F3.opPattern","COPY",FACE,{"derivedFrom":subQ1,"instanceName":"68"}),makeQuery(id+"F3.opPattern","COPY",FACE,{"derivedFrom":subQ1,"instanceName":"69"}),makeQuery(id+"F3.opPattern","COPY",FACE,{"derivedFrom":subQ1,"instanceName":"70"}),makeQuery(id+"F3.opPattern","COPY",FACE,{"derivedFrom":subQ1,"instanceName":"71"}),makeQuery(id+"F3.opPattern","COPY",FACE,{"derivedFrom":subQ1,"instanceName":"72"}),makeQuery(id+"F3.opPattern","COPY",FACE,{"derivedFrom":subQ1,"instanceName":"73"}),makeQuery(id+"F3.opPattern","COPY",FACE,{"derivedFrom":subQ1,"instanceName":"74"}),makeQuery(id+"F3.opPattern","COPY",FACE,{"derivedFrom":subQ1,"instanceName":"75"}),makeQuery(id+"F3.opPattern","COPY",FACE,{"derivedFrom":subQ1,"instanceName":"76"}),makeQuery(id+"F3.opPattern","COPY",FACE,{"derivedFrom":subQ1,"instanceName":"77"}),makeQuery(id+"F3.opPattern","COPY",FACE,{"derivedFrom":subQ1,"instanceName":"78"}),makeQuery(id+"F3.opPattern","COPY",FACE,{"derivedFrom":subQ1,"instanceName":"79"}),makeQuery(id+"F3.opPattern","COPY",FACE,{"derivedFrom":subQ1,"instanceName":"80"}),makeQuery(id+"F3.opPattern","COPY",FACE,{"derivedFrom":subQ1,"instanceName":"81"}),makeQuery(id+"F3.opPattern","COPY",FACE,{"derivedFrom":subQ1,"instanceName":"82"}),makeQuery(id+"F3.opPattern","COPY",FACE,{"derivedFrom":subQ1,"instanceName":"83"})]});}
            extrude(context, id + "F7", {"entities" : qUnion([Q0]), "endBound" : BoundingType.UP_TO_SURFACE, "oppositeDirection" : true, "endBoundEntityFace" : qUnion([Q1]), "depth" : 25.4 * mm});
        }
        {
            var Q0;
            Q0=makeQuery(id+"F7.opExtrude","SWEPT_EDGE",EDGE,{"disambiguationData":[OSD([sQuery(id+"F6.wireOp",EDGE,"E12"),sQuery(id+"F6.wireOp",EDGE,"E16.0")])]});
            var Q1;
            Q1=makeQuery(id+"F7.opExtrude","SWEPT_EDGE",EDGE,{"disambiguationData":[OSD([sQuery(id+"F6.wireOp",EDGE,"E11"),sQuery(id+"F6.wireOp",EDGE,"E16.0")])]});
            var Q2;
            Q2=makeQuery(id+"F7.opExtrude","SWEPT_EDGE",EDGE,{"disambiguationData":[OSD([sQuery(id+"F6.wireOp",EDGE,"E11"),sQuery(id+"F6.wireOp",EDGE,"E15.0")])]});
            var Q3;
            Q3=makeQuery(id+"F7.opExtrude","SWEPT_EDGE",EDGE,{"disambiguationData":[OSD([sQuery(id+"F6.wireOp",EDGE,"E12"),sQuery(id+"F6.wireOp",EDGE,"E15.0")])]});
            fillet(context, id + "F8", {"entities" : qUnion([Q0, Q1, Q2, Q3]), "radius" : 5.08 * mm, "tangentPropagation" : true, "allowEdgeOverflow" : false});
        }
        {
            var Q0;
            Q0=makeQuery(id+"F7.opExtrude","SWEPT_BODY",BODY,{"disambiguationData":[OSD([sQuery(id+"F6.wireOp",EDGE,"E11"),sQuery(id+"F6.wireOp",EDGE,"E12"),sQuery(id+"F6.wireOp",EDGE,"E15.0"),sQuery(id+"F6.wireOp",EDGE,"E16.0")])]});
            var Q1;
            Q1=makeQuery(id+"F5.boolean.opBoolean","COPY",FACE,{"derivedFrom":makeQuery(id+"F5.opExtrude","SWEPT_FACE",FACE,{"disambiguationData":[OSD([sQuery(id+"F4.wireOp",EDGE,"E10")])]})});
            circularPattern(context, id + "F9", {"operationType" : NewBodyOperationType.REMOVE, "entities" : qUnion([Q0]), "axis" : qUnion([Q1]), "angle" : 360 * degree, "instanceCount" : round(6), "equalSpace" : true});
        }
    });
